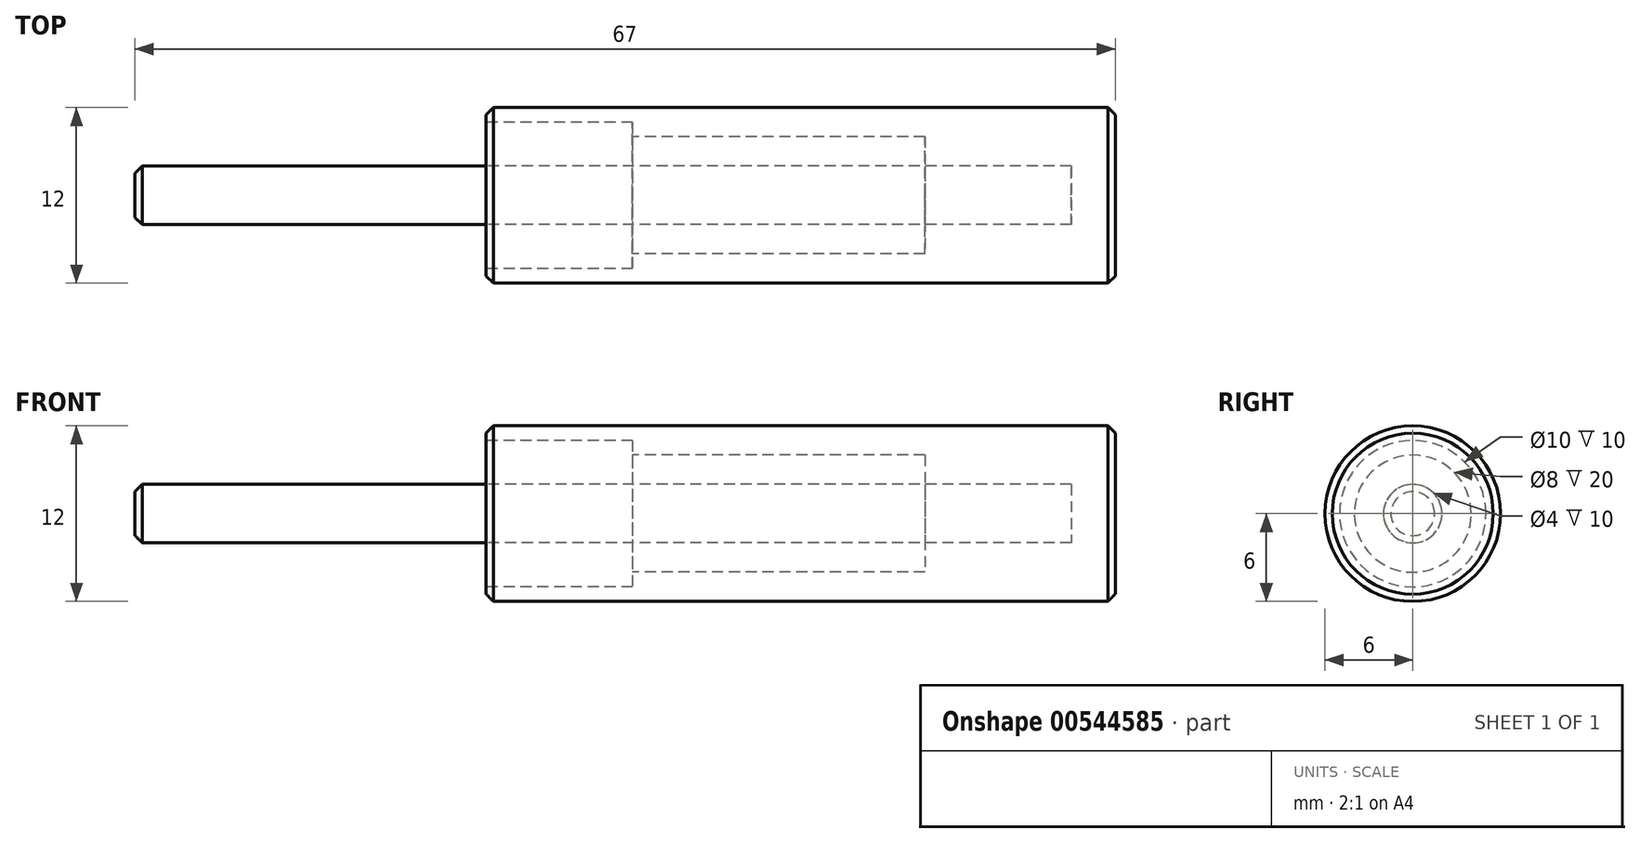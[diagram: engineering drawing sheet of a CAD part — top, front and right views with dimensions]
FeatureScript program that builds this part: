
annotation { "Feature Type Name" : "Feature", "Feature Type Description" : "" }
export const myFeature = defineFeature(function(context is Context, id is Id, definition is map)
    precondition{}
    {
        {
            var Q0;
            Q0=qCreatedBy(makeId("Top.planeOp"),FACE);
            var sketch = newSketch(context, id + "F0", { "sketchPlane" : qUnion([Q0])});
            skLineSegment(sketch, "E0", {"start": v(0, 6) * mm, "end": v(43, 6) * mm});
            skLineSegment(sketch, "E1", {"start": v(43, 6) * mm, "end": v(43, 0) * mm});
            skLineSegment(sketch, "E2", {"start": v(0, 6) * mm, "end": v(0, 5) * mm});
            skLineSegment(sketch, "E3", {"start": v(0, 5) * mm, "end": v(10, 5) * mm});
            skLineSegment(sketch, "E4", {"start": v(10, 5) * mm, "end": v(10, 4) * mm});
            skLineSegment(sketch, "E5", {"start": v(10, 4) * mm, "end": v(30, 4) * mm});
            skLineSegment(sketch, "E6", {"start": v(30, 4) * mm, "end": v(30, 2) * mm});
            skLineSegment(sketch, "E7", {"start": v(30, 2) * mm, "end": v(40, 2) * mm});
            skLineSegment(sketch, "E8", {"start": v(40, 2) * mm, "end": v(40, 0) * mm});
            skLineSegment(sketch, "E9", {"start": v(40, 0) * mm, "end": v(43, 0) * mm});
            skLineSegment(sketch, "E10", {"start": v(0, 0) * mm, "end": v(59.7, 0) * mm, "construction": true});
            skSolve(sketch);
        }
        {
            var Q0;
            Q0=makeQuery(id+"F0.imprint","IMPRINT",FACE,{"disambiguationData":[TD([[makeQuery(id+"F0.imprint","IMPRINT",EDGE,{"derivedFrom":sQuery(id+"F0.wireOp",EDGE,"E0")}),-1.0]])]});
            var Q1;
            Q1=sQuery(id+"F0.wireOp",EDGE,"E10");
            revolve(context, id + "F1", {"entities" : qUnion([Q0]), "axis" : qUnion([Q1]), "revolveType" : RevolveType.FULL});
        }
        {
            var Q0;
            Q0=makeQuery(id+"F1.opRevolve","SWEPT_EDGE",EDGE,{"disambiguationData":[OSD([sQuery(id+"F0.wireOp",EDGE,"E0"),sQuery(id+"F0.wireOp",EDGE,"E2")])]});
            var Q1;
            Q1=makeQuery(id+"F1.opRevolve","SWEPT_EDGE",EDGE,{"disambiguationData":[OSD([sQuery(id+"F0.wireOp",EDGE,"E0"),sQuery(id+"F0.wireOp",EDGE,"E1")])]});
            chamfer(context, id + "F2", {"entities" : qUnion([Q0, Q1]), "width" : 0.5 * mm, "tangentPropagation" : true});
        }
        {
            var Q0;
            Q0=qCreatedBy(makeId("Top.planeOp"),FACE);
            var sketch = newSketch(context, id + "F3", { "sketchPlane" : qUnion([Q0])});
            skLineSegment(sketch, "E11", {"start": v(0, 6) * mm, "end": v(43, 6) * mm, "construction": true});
            skLineSegment(sketch, "E12", {"start": v(43, 6) * mm, "end": v(43, -3.1) * mm, "construction": true});
            skLineSegment(sketch, "E13", {"start": v(0, 6) * mm, "end": v(0, 5) * mm, "construction": true});
            skLineSegment(sketch, "E14", {"start": v(0, 5) * mm, "end": v(10, 5) * mm, "construction": true});
            skLineSegment(sketch, "E15", {"start": v(10, 5) * mm, "end": v(10, 4) * mm, "construction": true});
            skLineSegment(sketch, "E16", {"start": v(10, 4) * mm, "end": v(30, 4) * mm, "construction": true});
            skLineSegment(sketch, "E17", {"start": v(30, 4) * mm, "end": v(30, 2) * mm, "construction": true});
            skLineSegment(sketch, "E18", {"start": v(30, 2) * mm, "end": v(40, 2) * mm, "construction": true});
            skLineSegment(sketch, "E19", {"start": v(40, 2) * mm, "end": v(40, -3.1) * mm, "construction": true});
            skLineSegment(sketch, "E20", {"start": v(40, -3.1) * mm, "end": v(43, -3.1) * mm, "construction": true});
            skLineSegment(sketch, "E21", {"start": v(0, 0) * mm, "end": v(59.7, 0) * mm, "construction": true});
            skLineSegment(sketch, "E22", {"start": v(40, 2) * mm, "end": v(-24, 2) * mm});
            skLineSegment(sketch, "E23", {"start": v(-24, 2) * mm, "end": v(-24, 0) * mm});
            skLineSegment(sketch, "E24", {"start": v(-24, 0) * mm, "end": v(40, 0) * mm});
            skLineSegment(sketch, "E25", {"start": v(40, 0) * mm, "end": v(40, 2) * mm});
            skSolve(sketch);
        }
        {
            var Q0;
            Q0=makeQuery(id+"F3.imprint","IMPRINT",FACE,{"disambiguationData":[TD([[makeQuery(id+"F3.imprint","IMPRINT",EDGE,{"derivedFrom":sQuery(id+"F3.wireOp",EDGE,"E22")}),1.0]])]});
            var Q1;
            Q1=sQuery(id+"F3.wireOp",EDGE,"E24");
            revolve(context, id + "F4", {"entities" : qUnion([Q0]), "axis" : qUnion([Q1]), "revolveType" : RevolveType.FULL});
        }
        {
            var Q0;
            Q0=makeQuery(id+"F4.opRevolve","SWEPT_EDGE",EDGE,{"disambiguationData":[OSD([sQuery(id+"F3.wireOp",EDGE,"E22"),sQuery(id+"F3.wireOp",EDGE,"E23")])]});
            chamfer(context, id + "F5", {"entities" : qUnion([Q0]), "width" : 0.5 * mm, "tangentPropagation" : true});
        }
    });
